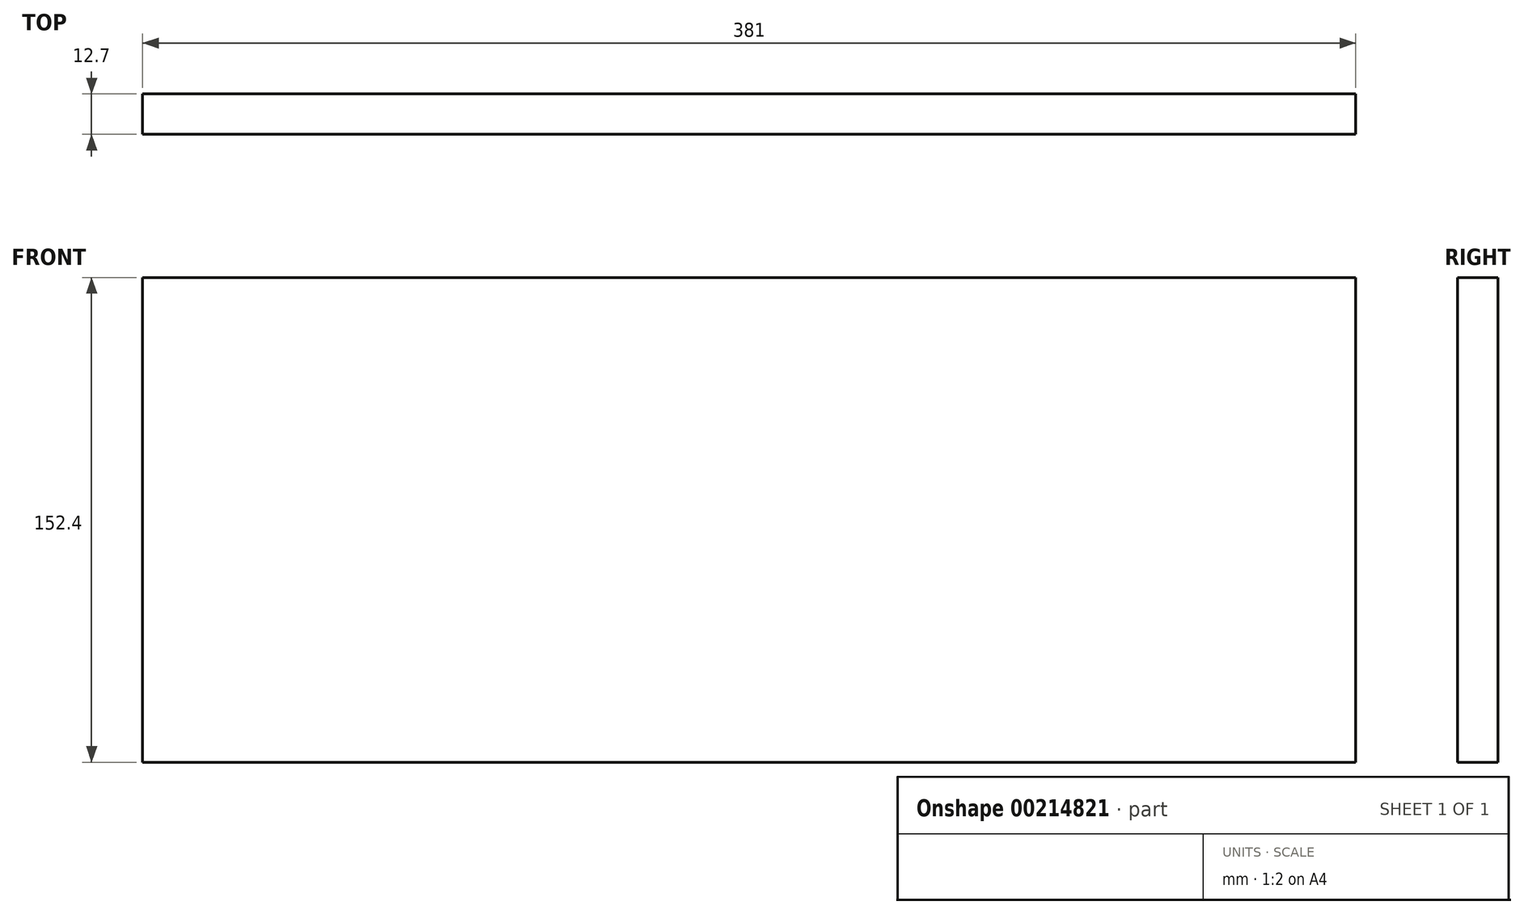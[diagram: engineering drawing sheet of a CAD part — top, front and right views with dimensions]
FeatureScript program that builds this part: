
annotation { "Feature Type Name" : "Feature", "Feature Type Description" : "" }
export const myFeature = defineFeature(function(context is Context, id is Id, definition is map)
    precondition{}
    {
        {
            var Q0;
            Q0=qCreatedBy(makeId("Front.planeOp"),FACE);
            var sketch = newSketch(context, id + "F0", { "sketchPlane" : qUnion([Q0])});
            skLineSegment(sketch, "E0.bottom", {"start": v(0, 0) * mm, "end": v(381, 0) * mm});
            skLineSegment(sketch, "E0.top", {"start": v(0, -152.4) * mm, "end": v(381, -152.4) * mm});
            skLineSegment(sketch, "E0.left", {"start": v(0, 0) * mm, "end": v(0, -152.4) * mm});
            skLineSegment(sketch, "E0.right", {"start": v(381, 0) * mm, "end": v(381, -152.4) * mm});
            skSolve(sketch);
        }
        {
            var Q0;
            Q0=makeQuery(id+"F0.imprint","IMPRINT",FACE,{"disambiguationData":[TD([[makeQuery(id+"F0.imprint","IMPRINT",EDGE,{"derivedFrom":sQuery(id+"F0.wireOp",EDGE,"E0.bottom")}),-1.0]])]});
            extrude(context, id + "F1", {"entities" : qUnion([Q0]), "depth" : 12.7 * mm});
        }
    });
